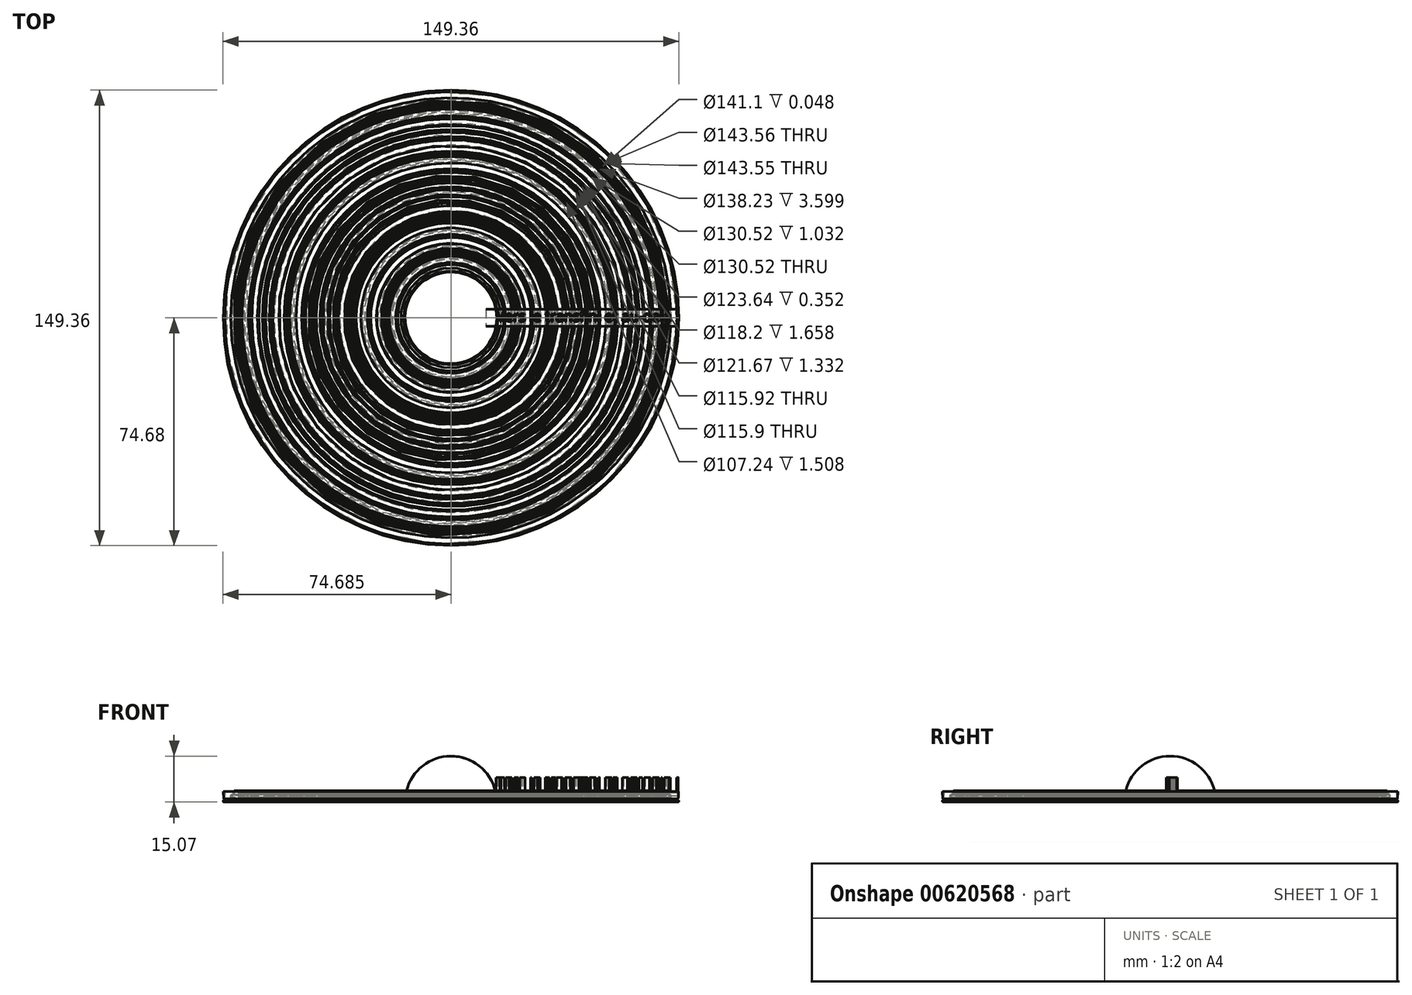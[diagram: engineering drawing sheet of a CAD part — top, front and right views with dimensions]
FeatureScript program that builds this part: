
annotation { "Feature Type Name" : "Feature", "Feature Type Description" : "" }
export const myFeature = defineFeature(function(context is Context, id is Id, definition is map)
    precondition{}
    {
        {
            var Q0;
            Q0=qCreatedBy(makeId("Front.planeOp"),FACE);
            var sketch = newSketch(context, id + "F0", { "sketchPlane" : qUnion([Q0])});
            skPoint(sketch, "E0", {"position": v(-24.08, 19.12) * mm});
            skText(sketch, "E1", { "text": "Vers le transfini et au-delà !", "fontName": "OpenSans-Regular.ttf"});
            skLineSegment(sketch, "E2", {"start": v(-9.07, 15.8) * mm, "end": v(-24.07, 15.8) * mm});
            skLineSegment(sketch, "E3", {"start": v(-9.45, 15.8) * mm, "end": v(-24.07, 15.8) * mm});
            skLineSegment(sketch, "E4", {"start": v(-24.07, 15.8) * mm, "end": v(-24.07, 30.8) * mm});
            skArc(sketch, "E5", {"start": v(-9.07, 15.8) * mm, "mid": v(-13.46, 26.4) * mm, "end": v(-24.07, 30.8) * mm});
            skLineSegment(sketch, "E6", {"start": v(-24.07, 30.8) * mm, "end": v(-24.07, 15.8) * mm});
            const initialGuessF0  = {"E1": [-0.00907, 0.0158, 1, 0, 0.00341]};
            skSetInitialGuess(sketch, initialGuessF0);
            skSolve(sketch);
        }
        {
            var Q0;
            Q0 = qSketchRegion(id + "F0", true);
            var Q1;
            Q1=sQuery(id+"F0.wireOp",EDGE,"E6");
            revolve(context, id + "F1", {"entities" : qUnion([Q0]), "axis" : qUnion([Q1]), "revolveType" : RevolveType.FULL});
        }
        {
            var Q0;
            Q0=makeQuery(id+"F1.opRevolve","SWEPT_FACE",FACE,{"disambiguationData":[OSD([sQuery(id+"F0.wireOp",EDGE,"E1.sketch_text.stroke-156")])]});
            var sketch = newSketch(context, id + "F2", { "sketchPlane" : qUnion([Q0])});
            skLineSegment(sketch, "E7.bottom", {"start": v(-12.58, 2.8) * mm, "end": v(50.14, 2.8) * mm});
            skLineSegment(sketch, "E7.top", {"start": v(-12.58, -2.8) * mm, "end": v(50.14, -2.8) * mm});
            skLineSegment(sketch, "E7.left", {"start": v(-12.58, 2.8) * mm, "end": v(-12.58, -2.8) * mm});
            skLineSegment(sketch, "E7.right", {"start": v(50.14, 2.8) * mm, "end": v(50.14, -2.8) * mm});
            skSolve(sketch);
        }
        {
            var Q0;
            Q0 = qSketchRegion(id + "F2", true);
            extrude(context, id + "F3", {"entities" : qUnion([Q0]), "endBound" : BoundingType.SYMMETRIC, "depth" : 1 * mm, "offsetDistance" : 25 * mm});
        }
        {
            var Q0;
            Q0=makeQuery(id+"F3.opExtrude","CAP_FACE",FACE,{"disambiguationData":[OSD([sQuery(id+"F2.wireOp",EDGE,"E7.bottom"),sQuery(id+"F2.wireOp",EDGE,"E7.top"),sQuery(id+"F2.wireOp",EDGE,"E7.left"),sQuery(id+"F2.wireOp",EDGE,"E7.right")])],"isStart":false});
            var sketch = newSketch(context, id + "F4", { "sketchPlane" : qUnion([Q0])});
            skText(sketch, "E8", { "text": "Vers le transfini et au-delà !", "fontName": "OpenSans-Regular.ttf"});
            const initialGuessF4  = {"E8": [-0.00924, -0.00119, 1, 0, 0.00341]};
            skSetInitialGuess(sketch, initialGuessF4);
            skSolve(sketch);
        }
        {
            var Q0;
            Q0 = qSketchRegion(id + "F4", true);
            extrude(context, id + "F5", {"entities" : qUnion([Q0]), "depth" : 5 * mm, "offsetDistance" : 25 * mm});
        }
    });
